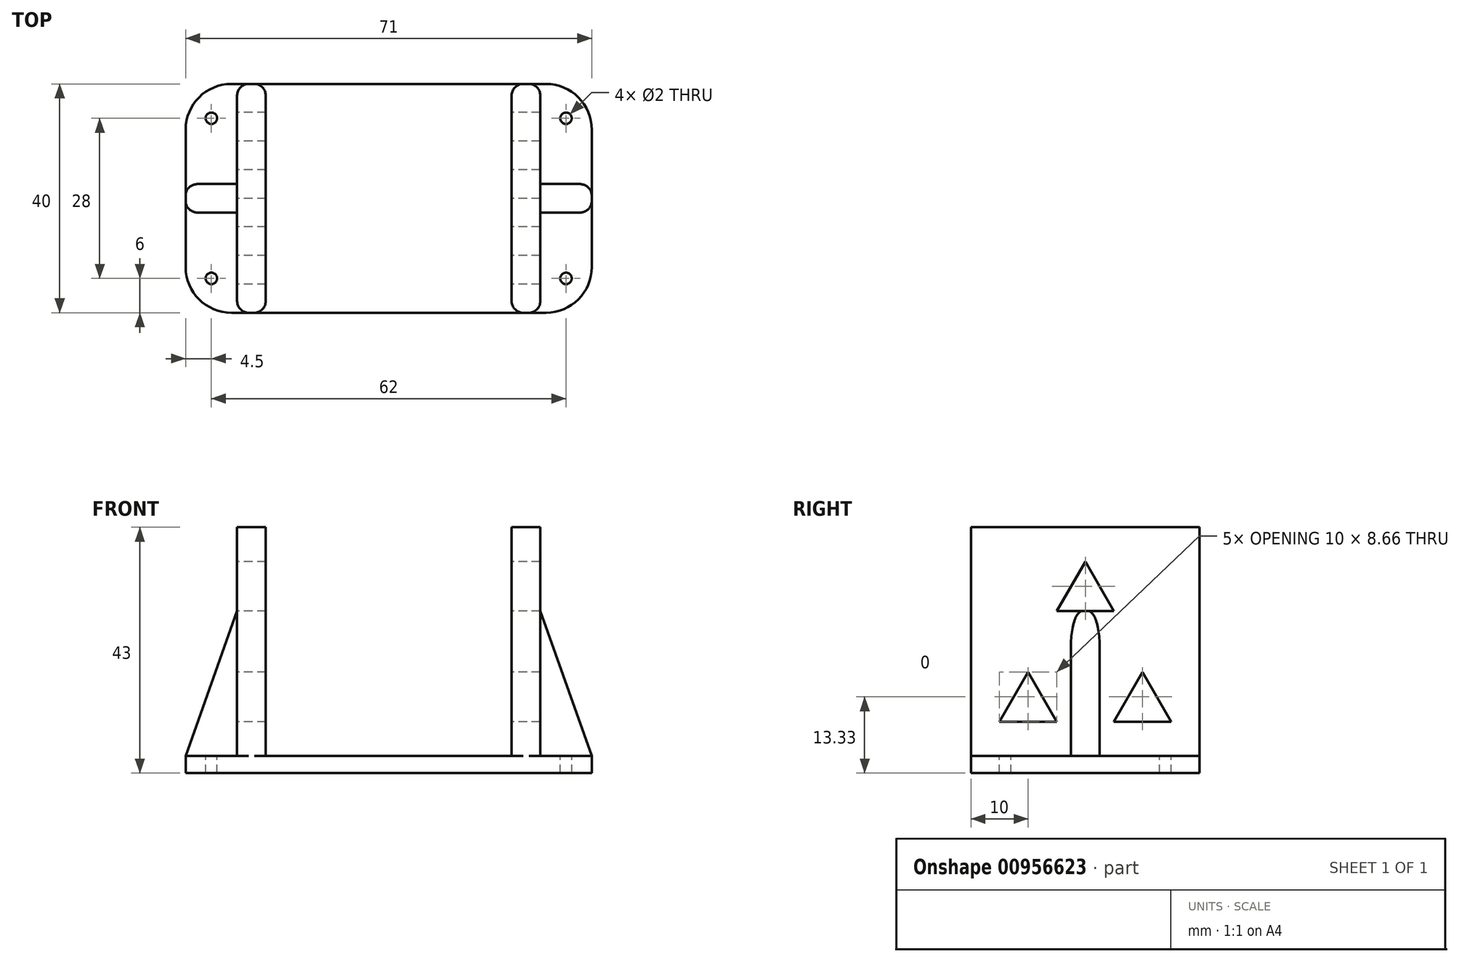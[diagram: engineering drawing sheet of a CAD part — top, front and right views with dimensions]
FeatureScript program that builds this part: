
annotation { "Feature Type Name" : "Feature", "Feature Type Description" : "" }
export const myFeature = defineFeature(function(context is Context, id is Id, definition is map)
    precondition{}
    {
        {
            var Q0;
            Q0=qCreatedBy(makeId("Top.planeOp"),FACE);
            var sketch = newSketch(context, id + "F0", { "sketchPlane" : qUnion([Q0])});
            skLineSegment(sketch, "E0.bottom", {"start": v(0, 0) * mm, "end": v(71, 0) * mm});
            skLineSegment(sketch, "E0.top", {"start": v(0, -40) * mm, "end": v(71, -40) * mm});
            skLineSegment(sketch, "E0.left", {"start": v(0, 0) * mm, "end": v(0, -40) * mm});
            skLineSegment(sketch, "E0.right", {"start": v(71, 0) * mm, "end": v(71, -40) * mm});
            skSolve(sketch);
        }
        {
            var Q0;
            Q0 = qSketchRegion(id + "F0", true);
            extrude(context, id + "F1", {"entities" : qUnion([Q0]), "depth" : 3 * mm, "offsetDistance" : 25 * mm});
        }
        {
            var Q0;
            Q0=makeQuery(id+"F1.opExtrude","CAP_FACE",FACE,{"disambiguationData":[OSD([sQuery(id+"F0.wireOp",EDGE,"E0.bottom"),sQuery(id+"F0.wireOp",EDGE,"E0.top"),sQuery(id+"F0.wireOp",EDGE,"E0.left"),sQuery(id+"F0.wireOp",EDGE,"E0.right")])],"isStart":false});
            var sketch = newSketch(context, id + "F2", { "sketchPlane" : qUnion([Q0])});
            skLineSegment(sketch, "E1.bottom", {"start": v(9, 0) * mm, "end": v(14, 0) * mm});
            skLineSegment(sketch, "E1.top", {"start": v(9, -40) * mm, "end": v(14, -40) * mm});
            skLineSegment(sketch, "E1.left", {"start": v(9, 0) * mm, "end": v(9, -40) * mm});
            skLineSegment(sketch, "E1.right", {"start": v(14, 0) * mm, "end": v(14, -40) * mm});
            skLineSegment(sketch, "E2.bottom", {"start": v(57, 0) * mm, "end": v(62, 0) * mm});
            skLineSegment(sketch, "E2.top", {"start": v(57, -40) * mm, "end": v(62, -40) * mm});
            skLineSegment(sketch, "E2.left", {"start": v(57, 0) * mm, "end": v(57, -40) * mm});
            skLineSegment(sketch, "E2.right", {"start": v(62, 0) * mm, "end": v(62, -40) * mm});
            skLineSegment(sketch, "E3", {"start": v(62, 0) * mm, "end": v(71, 0) * mm});
            skLineSegment(sketch, "E4", {"start": v(0, 0) * mm, "end": v(9, 0) * mm});
            skSolve(sketch);
        }
        {
            var Q0;
            Q0=makeQuery(id+"F2.imprint","IMPRINT",FACE,{"disambiguationData":[TD([[makeQuery(id+"F2.imprint","IMPRINT",EDGE,{"derivedFrom":sQuery(id+"F2.wireOp",EDGE,"E1.bottom")}),-1.0]])]});
            var Q1;
            Q1=makeQuery(id+"F2.imprint","IMPRINT",FACE,{"disambiguationData":[TD([[makeQuery(id+"F2.imprint","IMPRINT",EDGE,{"derivedFrom":sQuery(id+"F2.wireOp",EDGE,"E2.bottom")}),-1.0]])]});
            extrude(context, id + "F3", {"entities" : qUnion([Q0, Q1]), "operationType" : NewBodyOperationType.ADD, "depth" : 40 * mm, "offsetDistance" : 25 * mm});
        }
        {
            var Q0;
            {var subQ0=sQuery(id+"F0.wireOp",EDGE,"E0.left");var subQ1=sQuery(id+"F0.wireOp",EDGE,"E0.top");var subQ2=sQuery(id+"F0.wireOp",EDGE,"E0.bottom");Q0=makeQuery(id+"F3.boolean.opBoolean","SPLIT",FACE,{"disambiguationData":[TD([makeQuery(id+"F1.opExtrude","SWEPT_FACE",FACE,{"disambiguationData":[OSD([subQ0])]})])],"derivedFrom":makeQuery(id+"F1.opExtrude","CAP_FACE",FACE,{"disambiguationData":[OSD([subQ2,subQ1,subQ0,sQuery(id+"F0.wireOp",EDGE,"E0.right")])],"isStart":false})});}
            var sketch = newSketch(context, id + "F4", { "sketchPlane" : qUnion([Q0])});
            skLineSegment(sketch, "E5", {"start": v(4.5, 0) * mm, "end": v(4.5, -40) * mm, "construction": true});
            skLineSegment(sketch, "E6", {"start": v(66.5, 0) * mm, "end": v(66.5, -40) * mm, "construction": true});
            skCircle(sketch, "E7", {"center": v(4.5, -6) * mm, "radius": 1 * mm});
            skCircle(sketch, "E8", {"center": v(4.5, -34) * mm, "radius": 1 * mm});
            skCircle(sketch, "E9", {"center": v(66.5, -6) * mm, "radius": 1 * mm});
            skCircle(sketch, "E10", {"center": v(66.5, -34) * mm, "radius": 1 * mm});
            skSolve(sketch);
        }
        {
            var Q0;
            Q0 = qSketchRegion(id + "F4", true);
            extrude(context, id + "F5", {"entities" : qUnion([Q0]), "operationType" : NewBodyOperationType.REMOVE, "endBound" : BoundingType.THROUGH_ALL, "oppositeDirection" : true, "depth" : 25 * mm, "offsetDistance" : 25 * mm});
        }
        {
            var Q0;
            Q0=makeQuery(id+"F3.opExtrude","SWEPT_FACE",FACE,{"disambiguationData":[OSD([sQuery(id+"F2.wireOp",EDGE,"E1.left")])]});
            var sketch = newSketch(context, id + "F6", { "sketchPlane" : qUnion([Q0])});
            skLineSegment(sketch, "E11", {"start": v(5, 9) * mm, "end": v(15, 9) * mm});
            skLineSegment(sketch, "E12", {"start": v(15, 9) * mm, "end": v(10, 17.66) * mm});
            skLineSegment(sketch, "E13", {"start": v(10, 17.66) * mm, "end": v(5, 9) * mm});
            skLineSegment(sketch, "E14", {"start": v(20, 37) * mm, "end": v(15, 28.34) * mm});
            skLineSegment(sketch, "E15", {"start": v(15, 28.34) * mm, "end": v(25, 28.34) * mm});
            skLineSegment(sketch, "E16", {"start": v(25, 28.34) * mm, "end": v(20, 37) * mm});
            skLineSegment(sketch, "E17", {"start": v(30, 17.66) * mm, "end": v(25, 9) * mm});
            skLineSegment(sketch, "E18", {"start": v(25, 9) * mm, "end": v(35, 9) * mm});
            skLineSegment(sketch, "E19", {"start": v(35, 9) * mm, "end": v(30, 17.66) * mm});
            skLineSegment(sketch, "E20", {"start": v(20, 43) * mm, "end": v(20, 3) * mm, "construction": true});
            skSolve(sketch);
        }
        {
            var Q0;
            Q0 = qSketchRegion(id + "F6", true);
            extrude(context, id + "F7", {"entities" : qUnion([Q0]), "operationType" : NewBodyOperationType.REMOVE, "endBound" : BoundingType.THROUGH_ALL, "oppositeDirection" : true, "depth" : 25 * mm, "offsetDistance" : 25 * mm});
        }
        {
            var Q0;
            Q0=makeQuery(id+"F3.opExtrude","CAP_EDGE",EDGE,{"disambiguationData":[OSD([sQuery(id+"F2.wireOp",EDGE,"E2.right")])],"isStart":false});
            cPoint(context, id + "F8", {"entities" : qUnion([Q0]), "parameter" : 0.5});
        }
        {
            var Q0;
            Q0=makeQuery(id+"F3.opExtrude","CAP_EDGE",EDGE,{"disambiguationData":[OSD([sQuery(id+"F2.wireOp",EDGE,"E2.right")])],"isStart":true});
            cPoint(context, id + "F9", {"entities" : qUnion([Q0]), "parameter" : 0.5});
        }
        {
            var Q0;
            Q0=makeQuery(id+"F3.opExtrude","CAP_EDGE",EDGE,{"disambiguationData":[OSD([sQuery(id+"F2.wireOp",EDGE,"E1.right")])],"isStart":false});
            cPoint(context, id + "F10", {"entities" : qUnion([Q0]), "parameter" : 0.5});
        }
        {
            var Q0;
            Q0 = qCreatedBy(id + "F8" ,VERTEX);
            var Q1;
            Q1 = qCreatedBy(id + "F9" ,VERTEX);
            var Q2;
            Q2 = qCreatedBy(id + "F10" ,VERTEX);
            cPlane(context, id + "F11", {"entities" : qUnion([Q0, Q1, Q2]), "cplaneType" : CPlaneType.THREE_POINT, "offset" : 25 * mm, "width" : 150 * mm, "height" : 150 * mm});
        }
        {
            var Q0;
            Q0=qCreatedBy(id+"F11.planeOp",FACE);
            var sketch = newSketch(context, id + "F12", { "sketchPlane" : qUnion([Q0])});
            skLineSegment(sketch, "E21", {"start": v(62, 3) * mm, "end": v(71, 3) * mm});
            skLineSegment(sketch, "E22", {"start": v(71, 3) * mm, "end": v(62, 28.34) * mm});
            skLineSegment(sketch, "E23", {"start": v(62, 28.34) * mm, "end": v(62, 3) * mm});
            skLineSegment(sketch, "E24", {"start": v(9, 3) * mm, "end": v(0, 3) * mm});
            skLineSegment(sketch, "E25", {"start": v(0, 3) * mm, "end": v(9, 28.34) * mm});
            skLineSegment(sketch, "E26", {"start": v(9, 28.34) * mm, "end": v(9, 3) * mm});
            skSolve(sketch);
        }
        {
            var Q0;
            Q0 = qSketchRegion(id + "F12", true);
            extrude(context, id + "F13", {"entities" : qUnion([Q0]), "operationType" : NewBodyOperationType.ADD, "endBound" : BoundingType.SYMMETRIC, "depth" : 5 * mm, "offsetDistance" : 25 * mm});
        }
        {
            var Q0;
            Q0=makeQuery(id+"F1.opExtrude","SWEPT_EDGE",EDGE,{"disambiguationData":[OSD([sQuery(id+"F0.wireOp",EDGE,"E0.bottom"),sQuery(id+"F0.wireOp",EDGE,"E0.right")])]});
            var Q1;
            Q1=makeQuery(id+"F1.opExtrude","SWEPT_EDGE",EDGE,{"disambiguationData":[OSD([sQuery(id+"F0.wireOp",EDGE,"E0.bottom"),sQuery(id+"F0.wireOp",EDGE,"E0.left")])]});
            var Q2;
            Q2=makeQuery(id+"F1.opExtrude","SWEPT_EDGE",EDGE,{"disambiguationData":[OSD([sQuery(id+"F0.wireOp",EDGE,"E0.top"),sQuery(id+"F0.wireOp",EDGE,"E0.right")])]});
            var Q3;
            Q3=makeQuery(id+"F1.opExtrude","SWEPT_EDGE",EDGE,{"disambiguationData":[OSD([sQuery(id+"F0.wireOp",EDGE,"E0.top"),sQuery(id+"F0.wireOp",EDGE,"E0.left")])]});
            fillet(context, id + "F14", {"entities" : qUnion([Q0, Q1, Q2, Q3]), "radius" : 8 * mm, "tangentPropagation" : true, "allowEdgeOverflow" : false});
        }
        {
            var Q0;
            Q0=makeQuery(id+"F3.opExtrude","SWEPT_EDGE",EDGE,{"disambiguationData":[OSD([sQuery(id+"F0.wireOp",EDGE,"E0.top"),sQuery(id+"F2.wireOp",EDGE,"E1.top"),sQuery(id+"F2.wireOp",EDGE,"E1.left")])]});
            var Q1;
            Q1=makeQuery(id+"F3.opExtrude","SWEPT_EDGE",EDGE,{"disambiguationData":[OSD([sQuery(id+"F2.wireOp",EDGE,"E1.bottom"),sQuery(id+"F2.wireOp",EDGE,"E1.left"),sQuery(id+"F2.wireOp",EDGE,"E4")])]});
            var Q2;
            Q2=makeQuery(id+"F3.opExtrude","SWEPT_EDGE",EDGE,{"disambiguationData":[OSD([sQuery(id+"F0.wireOp",EDGE,"E0.top"),sQuery(id+"F2.wireOp",EDGE,"E2.top"),sQuery(id+"F2.wireOp",EDGE,"E2.right")])]});
            var Q3;
            Q3=makeQuery(id+"F3.opExtrude","SWEPT_EDGE",EDGE,{"disambiguationData":[OSD([sQuery(id+"F2.wireOp",EDGE,"E2.bottom"),sQuery(id+"F2.wireOp",EDGE,"E2.right"),sQuery(id+"F2.wireOp",EDGE,"E3")])]});
            var Q4;
            Q4=makeQuery(id+"F13.opExtrude","CAP_EDGE",EDGE,{"disambiguationData":[OSD([sQuery(id+"F12.wireOp",EDGE,"E25")])],"isStart":true});
            var Q5;
            Q5=makeQuery(id+"F13.opExtrude","CAP_EDGE",EDGE,{"disambiguationData":[OSD([sQuery(id+"F12.wireOp",EDGE,"E25")])],"isStart":false});
            var Q6;
            Q6=makeQuery(id+"F13.opExtrude","CAP_EDGE",EDGE,{"disambiguationData":[OSD([sQuery(id+"F12.wireOp",EDGE,"E22")])],"isStart":true});
            var Q7;
            Q7=makeQuery(id+"F13.opExtrude","CAP_EDGE",EDGE,{"disambiguationData":[OSD([sQuery(id+"F12.wireOp",EDGE,"E22")])],"isStart":false});
            var Q8;
            Q8=makeQuery(id+"F3.opExtrude","SWEPT_EDGE",EDGE,{"disambiguationData":[OSD([sQuery(id+"F0.wireOp",EDGE,"E0.bottom"),sQuery(id+"F2.wireOp",EDGE,"E2.bottom"),sQuery(id+"F2.wireOp",EDGE,"E2.left")])]});
            var Q9;
            Q9=makeQuery(id+"F3.opExtrude","SWEPT_EDGE",EDGE,{"disambiguationData":[OSD([sQuery(id+"F0.wireOp",EDGE,"E0.bottom"),sQuery(id+"F2.wireOp",EDGE,"E1.bottom"),sQuery(id+"F2.wireOp",EDGE,"E1.right")])]});
            var Q10;
            Q10=makeQuery(id+"F3.opExtrude","SWEPT_EDGE",EDGE,{"disambiguationData":[OSD([sQuery(id+"F0.wireOp",EDGE,"E0.top"),sQuery(id+"F2.wireOp",EDGE,"E2.top"),sQuery(id+"F2.wireOp",EDGE,"E2.left")])]});
            var Q11;
            Q11=makeQuery(id+"F3.opExtrude","SWEPT_EDGE",EDGE,{"disambiguationData":[OSD([sQuery(id+"F0.wireOp",EDGE,"E0.top"),sQuery(id+"F2.wireOp",EDGE,"E1.top"),sQuery(id+"F2.wireOp",EDGE,"E1.right")])]});
            fillet(context, id + "F15", {"entities" : qUnion([Q0, Q1, Q2, Q3, Q4, Q5, Q6, Q7, Q8, Q9, Q10, Q11]), "radius" : 2 * mm, "tangentPropagation" : true, "allowEdgeOverflow" : false});
        }
    });
